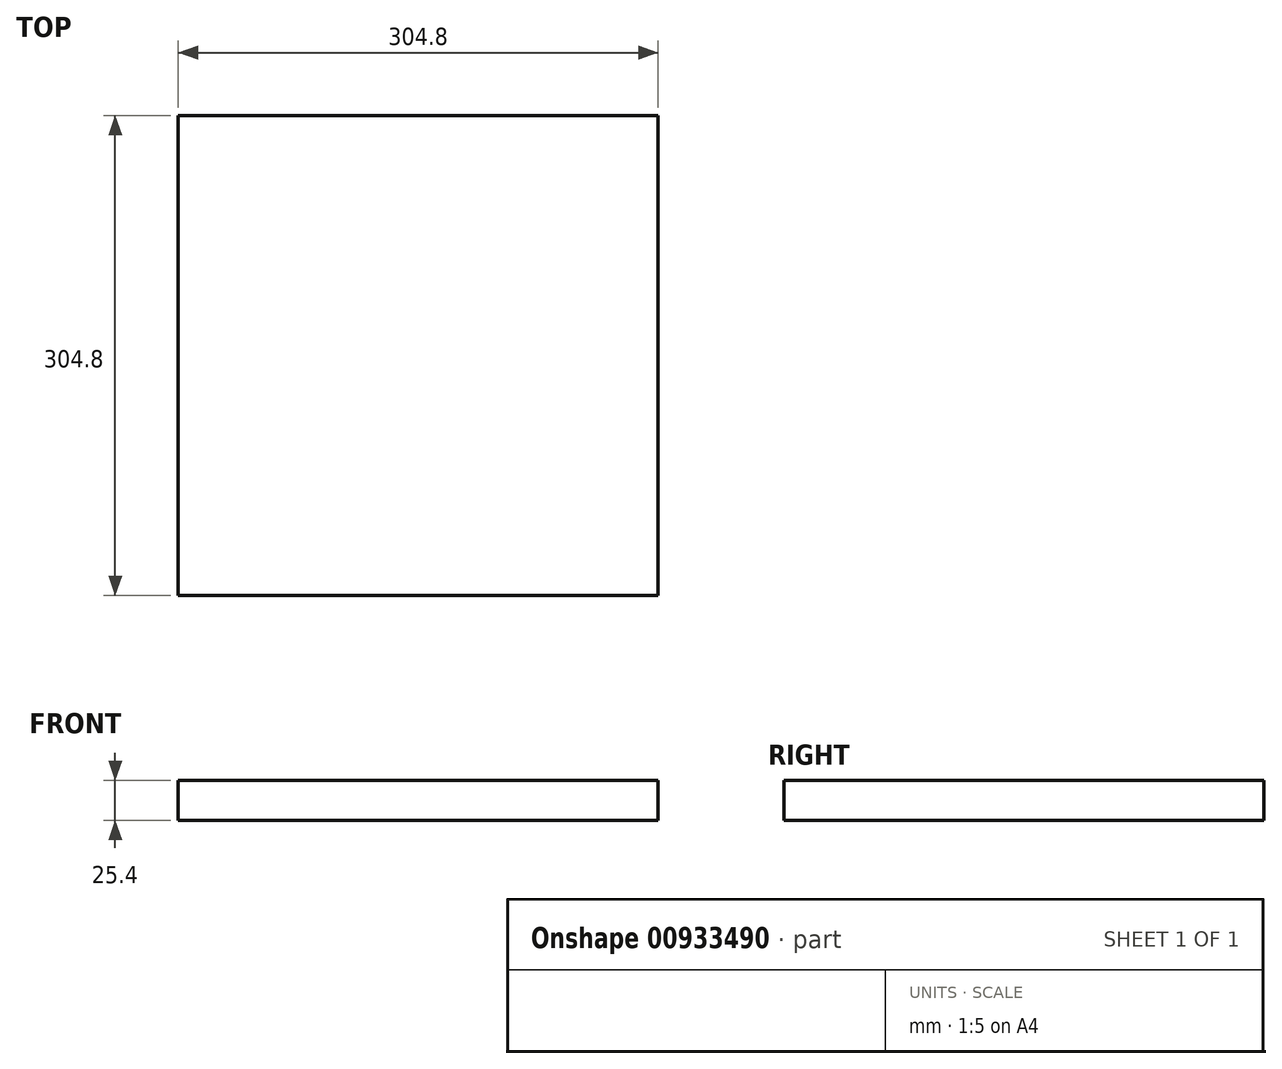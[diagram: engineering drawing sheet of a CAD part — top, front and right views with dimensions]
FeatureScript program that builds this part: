
annotation { "Feature Type Name" : "Feature", "Feature Type Description" : "" }
export const myFeature = defineFeature(function(context is Context, id is Id, definition is map)
    precondition{}
    {
        {
            var Q0;
            Q0=qCreatedBy(makeId("Top.planeOp"),FACE);
            var sketch = newSketch(context, id + "F0", { "sketchPlane" : qUnion([Q0])});
            skLineSegment(sketch, "E0.bottom", {"start": v(152.4, 152.4) * mm, "end": v(-152.4, 152.4) * mm});
            skLineSegment(sketch, "E0.top", {"start": v(152.4, -152.4) * mm, "end": v(-152.4, -152.4) * mm});
            skLineSegment(sketch, "E0.left", {"start": v(152.4, 152.4) * mm, "end": v(152.4, -152.4) * mm});
            skLineSegment(sketch, "E0.right", {"start": v(-152.4, 152.4) * mm, "end": v(-152.4, -152.4) * mm});
            skPoint(sketch, "E0.middle", {"position": v(0, 0) * mm});
            skSolve(sketch);
        }
        {
            var Q0;
            Q0=makeQuery(id+"F0.imprint","IMPRINT",FACE,{"disambiguationData":[TD([[makeQuery(id+"F0.imprint","IMPRINT",EDGE,{"derivedFrom":sQuery(id+"F0.wireOp",EDGE,"E0.bottom")}),1.0]])]});
            extrude(context, id + "F1", {"entities" : qUnion([Q0]), "depth" : 25.4 * mm, "offsetDistance" : 25.4 * mm});
        }
    });
